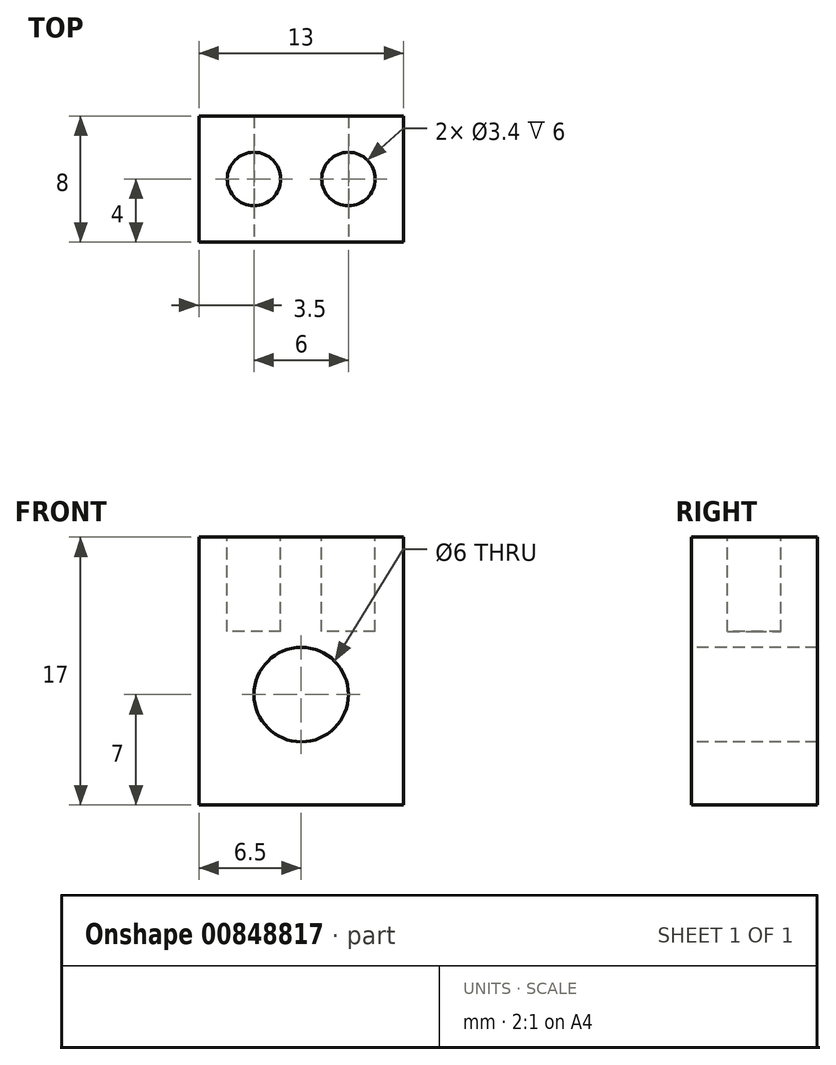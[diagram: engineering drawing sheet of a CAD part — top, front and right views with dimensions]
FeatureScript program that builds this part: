
annotation { "Feature Type Name" : "Feature", "Feature Type Description" : "" }
export const myFeature = defineFeature(function(context is Context, id is Id, definition is map)
    precondition{}
    {
        {
            var Q0;
            Q0=qCreatedBy(makeId("Front.planeOp"),FACE);
            var sketch = newSketch(context, id + "F0", { "sketchPlane" : qUnion([Q0])});
            skLineSegment(sketch, "E0.bottom", {"start": v(0, 0) * mm, "end": v(13, 0) * mm});
            skLineSegment(sketch, "E0.top", {"start": v(0, 17) * mm, "end": v(13, 17) * mm});
            skLineSegment(sketch, "E0.left", {"start": v(0, 0) * mm, "end": v(0, 17) * mm});
            skLineSegment(sketch, "E0.right", {"start": v(13, 0) * mm, "end": v(13, 17) * mm});
            skSolve(sketch);
        }
        {
            var Q0;
            Q0 = qSketchRegion(id + "F0", true);
            extrude(context, id + "F1", {"entities" : qUnion([Q0]), "depth" : 8 * mm, "offsetDistance" : 25 * mm});
        }
        {
            var Q0;
            Q0=makeQuery(id+"F1.opExtrude","SWEPT_FACE",FACE,{"disambiguationData":[OSD([sQuery(id+"F0.wireOp",EDGE,"E0.top")])]});
            var sketch = newSketch(context, id + "F2", { "sketchPlane" : qUnion([Q0])});
            skCircle(sketch, "E1", {"center": v(3.5, -4) * mm, "radius": 1.7 * mm});
            skCircle(sketch, "E2", {"center": v(9.5, -4) * mm, "radius": 1.7 * mm});
            skSolve(sketch);
        }
        {
            var Q0;
            Q0 = qSketchRegion(id + "F2", true);
            extrude(context, id + "F3", {"entities" : qUnion([Q0]), "operationType" : NewBodyOperationType.REMOVE, "oppositeDirection" : true, "depth" : 6 * mm, "offsetDistance" : 25 * mm});
        }
        {
            var Q0;
            Q0=makeQuery(id+"F1.opExtrude","CAP_FACE",FACE,{"disambiguationData":[OSD([sQuery(id+"F0.wireOp",EDGE,"E0.bottom"),sQuery(id+"F0.wireOp",EDGE,"E0.top"),sQuery(id+"F0.wireOp",EDGE,"E0.left"),sQuery(id+"F0.wireOp",EDGE,"E0.right")])],"isStart":false});
            var sketch = newSketch(context, id + "F4", { "sketchPlane" : qUnion([Q0])});
            skCircle(sketch, "E3", {"center": v(6.5, 7) * mm, "radius": 3 * mm});
            skSolve(sketch);
        }
        {
            var Q0;
            Q0 = qSketchRegion(id + "F4", true);
            extrude(context, id + "F5", {"entities" : qUnion([Q0]), "operationType" : NewBodyOperationType.REMOVE, "oppositeDirection" : true, "depth" : 25 * mm, "offsetDistance" : 25 * mm});
        }
    });
